# Revit family: SDP-855 IP-видеокамера_RV17_LOD400 (08.12.23)
name_source: partatom
category: Устройства связи
revit_build: Autodesk Revit 2017 (Build: 20170118_1100(x64)
units: mm (PartAtom-declared; Revit-internal decimal feet)

## family parameters
Всегда вертикально = Нет
На основе рабочей плоскости = Да
Общий = Нет
При загрузке вырезать с полостями = Нет
Размер круглого соединителя = Использовать диаметр
Сохранять ориентацию аннотаций = Нет
Тип детали = Нормальный
Точка расчета площади = Нет

## types (1)
- SDP-855 IP-видеокамера
    ADSK_URL страницы изделия = https://stilsoft.ru
    ADSK_Единица измерения = шт.
    ADSK_Завод-изготовитель = ООО «Основа Безопасности»
    ADSK_Количество = 1
    ADSK_Марка = CТАЕ.426459.046-03
    ADSK_Масса = 0.5
    ADSK_Наименование = IP-видеокамера SDP-855
    ADSK_Размер_Высота = 110 мм
    ADSK_Размер_ДиаметрИзделия = 140 мм
    d_короба = 20 мм
    Дальность ИК-подсветки, до, м = 30
    Диапазон рабочих температур, <unrecoverable-encoding: 5 bytes ef82b0d0a1> = от -40 до +50
    Матрица = 1/2.8" Progressive Scan CMOS
    Мощность = 9
    Напряжение = 12
    Объектив, мм = 2.8 – 12
    Отметка по умолчанию = 1219 мм
    Поддерживаемые протоколы = IPv4/IPv6, RTSP/RTP/RTCP, TCP/UDP, HTTP, HTTPS, DHCP, SNMP, DNS, FTP, 
DDNS, PPPoE, SMTP, ONVIF2.4.1
    Разрешение при частоте 25 кадр/сек, пикс. = 1920х1080
    Режим «День/ночь» = Механический ИК-фильтр с автопереключением
    Сетевой интерфейс = 1 RJ45 10М/100М Ethernet порт
    Скорость передачи = 50Кб/сек – 12МБ/сек
    Тип поддерживаемой карты памяти = SD-карта
    Угол обзора, ° = 26-86
    Управление = Веб-интерфейс, Stil-VL
    Формат сжатия = H.265, Н.264, MJPEG
    Чувствительность цвет, Люкс = 0,01 / F1.2
    Чувствительность ч/б, Люкс = 0,001 / F1.2
    Электронный затвор, сек. = 1/5-1/50000
